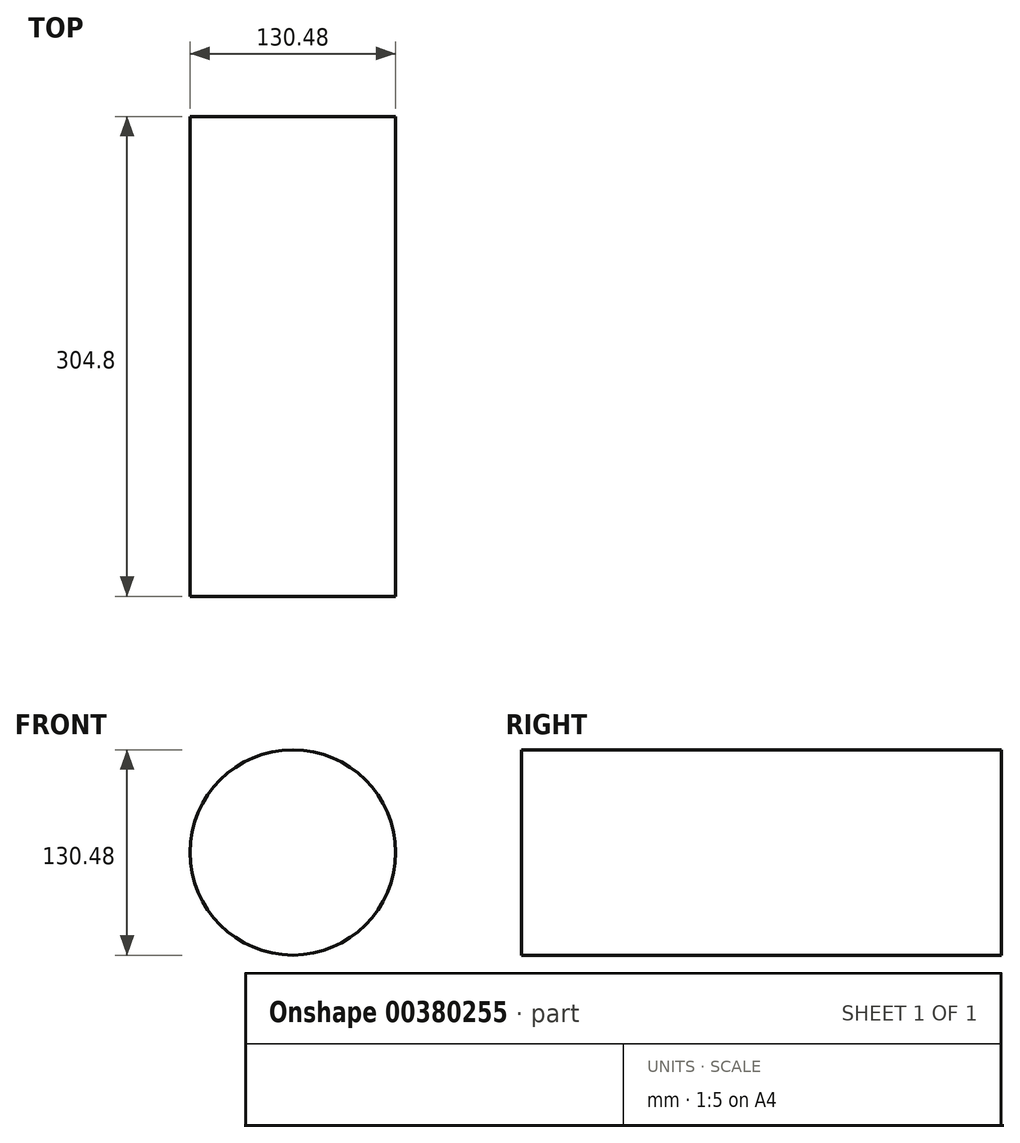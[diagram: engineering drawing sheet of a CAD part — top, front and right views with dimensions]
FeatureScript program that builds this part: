
annotation { "Feature Type Name" : "Feature", "Feature Type Description" : "" }
export const myFeature = defineFeature(function(context is Context, id is Id, definition is map)
    precondition{}
    {
        {
            var Q0;
            Q0=qCreatedBy(makeId("Front.planeOp"),FACE);
            var sketch = newSketch(context, id + "F0", { "sketchPlane" : qUnion([Q0])});
            skCircle(sketch, "E0", {"center": v(-270464.45, 115825.82) * mm, "radius": 65.24 * mm});
            skSolve(sketch);
        }
        {
            var Q0;
            Q0 = qSketchRegion(id + "F0", true);
            extrude(context, id + "F1", {"entities" : qUnion([Q0]), "oppositeDirection" : true, "depth" : 304.8 * mm});
        }
    });
